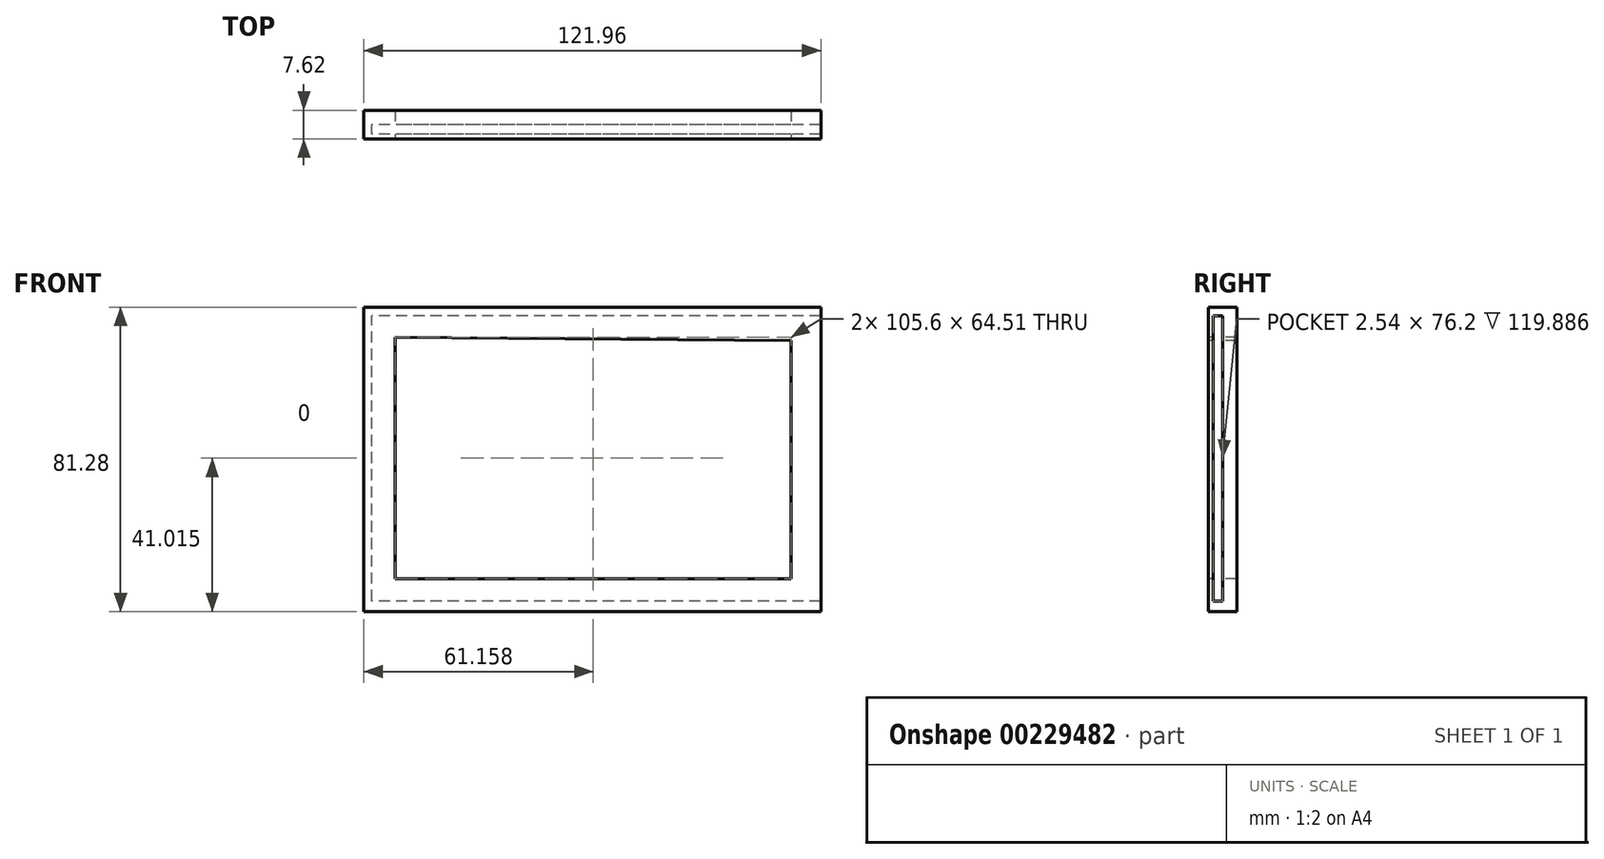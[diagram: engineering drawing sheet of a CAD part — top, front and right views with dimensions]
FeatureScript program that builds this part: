
annotation { "Feature Type Name" : "Feature", "Feature Type Description" : "" }
export const myFeature = defineFeature(function(context is Context, id is Id, definition is map)
    precondition{}
    {
        {
            var Q0;
            Q0=qCreatedBy(makeId("Front.planeOp"),FACE);
            var sketch = newSketch(context, id + "F0", { "sketchPlane" : qUnion([Q0])});
            skLineSegment(sketch, "E0.bottom", {"start": v(63.5, -38.1) * mm, "end": v(-63.5, -38.1) * mm});
            skLineSegment(sketch, "E0.top", {"start": v(63.5, 38.1) * mm, "end": v(-63.5, 38.1) * mm});
            skLineSegment(sketch, "E0.left", {"start": v(63.5, -38.1) * mm, "end": v(63.5, 38.1) * mm});
            skLineSegment(sketch, "E0.right", {"start": v(-63.5, -38.1) * mm, "end": v(-63.5, 38.1) * mm});
            skPoint(sketch, "E0.middle", {"position": v(0, 0) * mm});
            skSolve(sketch);
        }
        {
            var Q0;
            Q0=makeQuery(id+"F0.imprint","IMPRINT",FACE,{"disambiguationData":[TD([[makeQuery(id+"F0.imprint","IMPRINT",EDGE,{"derivedFrom":sQuery(id+"F0.wireOp",EDGE,"E0.bottom")}),-1.0]])]});
            extrude(context, id + "F1", {"entities" : qUnion([Q0]), "depth" : 2.54 * mm});
        }
        {
            var Q0;
            Q0=qCreatedBy(makeId("Front.planeOp"),FACE);
            var sketch = newSketch(context, id + "F2", { "sketchPlane" : qUnion([Q0])});
            skLineSegment(sketch, "E1.bottom", {"start": v(-65.57, -40.95) * mm, "end": v(56.39, -40.95) * mm});
            skLineSegment(sketch, "E1.top", {"start": v(-65.57, 40.33) * mm, "end": v(56.39, 40.33) * mm});
            skLineSegment(sketch, "E1.left", {"start": v(-65.57, -40.95) * mm, "end": v(-65.57, 40.33) * mm});
            skLineSegment(sketch, "E1.right", {"start": v(56.39, -40.95) * mm, "end": v(56.39, 40.33) * mm});
            skSolve(sketch);
        }
        {
            var Q0;
            Q0=makeQuery(id+"F2.imprint","IMPRINT",FACE,{"disambiguationData":[TD([[makeQuery(id+"F2.imprint","IMPRINT",EDGE,{"derivedFrom":sQuery(id+"F2.wireOp",EDGE,"E1.bottom")}),1.0]])]});
            extrude(context, id + "F3", {"entities" : qUnion([Q0]), "endBound" : BoundingType.SYMMETRIC, "depth" : 7.62 * mm});
        }
        {
            var Q0;
            Q0=makeQuery(id+"F3.opExtrude","CAP_FACE",FACE,{"disambiguationData":[OSD([sQuery(id+"F2.wireOp",EDGE,"E1.bottom"),sQuery(id+"F2.wireOp",EDGE,"E1.top"),sQuery(id+"F2.wireOp",EDGE,"E1.left"),sQuery(id+"F2.wireOp",EDGE,"E1.right")])],"isStart":false});
            var sketch = newSketch(context, id + "F4", { "sketchPlane" : qUnion([Q0])});
            skLineSegment(sketch, "E2", {"start": v(-57.21, 32.32) * mm, "end": v(-57.21, -32.19) * mm});
            skLineSegment(sketch, "E3", {"start": v(-57.21, -32.19) * mm, "end": v(48.39, -32.19) * mm});
            skLineSegment(sketch, "E4", {"start": v(48.39, -32.19) * mm, "end": v(48.39, 31.43) * mm});
            skLineSegment(sketch, "E5", {"start": v(48.39, 31.43) * mm, "end": v(-57.21, 32.32) * mm});
            skSolve(sketch);
        }
        {
            var Q0;
            Q0=makeQuery(id+"F4.imprint","IMPRINT",FACE,{"disambiguationData":[TD([[makeQuery(id+"F4.imprint","IMPRINT",EDGE,{"derivedFrom":sQuery(id+"F4.wireOp",EDGE,"E2")}),1.0]])]});
            extrude(context, id + "F5", {"entities" : qUnion([Q0]), "operationType" : NewBodyOperationType.REMOVE, "oppositeDirection" : true, "depth" : 25.4 * mm});
        }
        {
            var Q0;
            Q0=makeQuery(id+"F1.opExtrude","SWEPT_BODY",BODY,{"disambiguationData":[OSD([sQuery(id+"F0.wireOp",EDGE,"E0.bottom"),sQuery(id+"F0.wireOp",EDGE,"E0.top"),sQuery(id+"F0.wireOp",EDGE,"E0.left"),sQuery(id+"F0.wireOp",EDGE,"E0.right")])]});
            var Q1;
            Q1=makeQuery(id+"F3.opExtrude","SWEPT_BODY",BODY,{"disambiguationData":[OSD([sQuery(id+"F2.wireOp",EDGE,"E1.bottom"),sQuery(id+"F2.wireOp",EDGE,"E1.top"),sQuery(id+"F2.wireOp",EDGE,"E1.left"),sQuery(id+"F2.wireOp",EDGE,"E1.right")])]});
            booleanBodies(context, id + "F6", {"operationType" : BooleanOperationType.SUBTRACTION, "tools" : qUnion([Q0]), "targets" : qUnion([Q1])});
        }
    });
